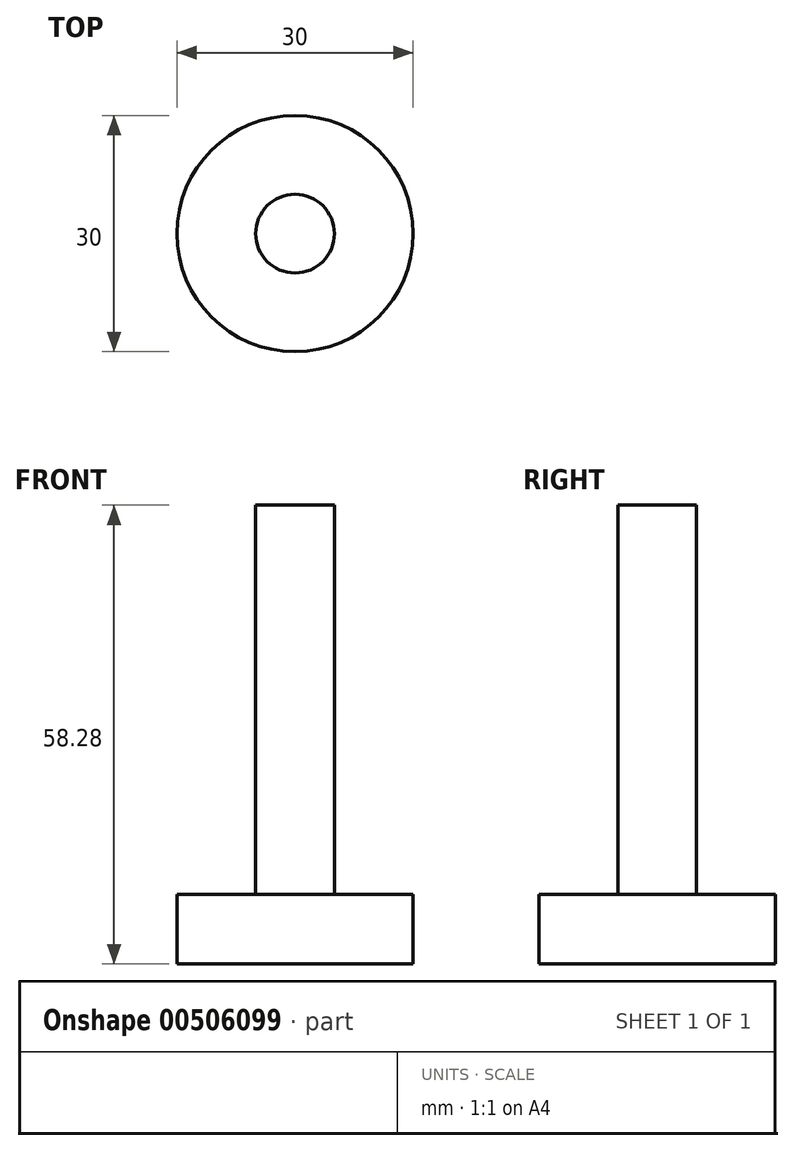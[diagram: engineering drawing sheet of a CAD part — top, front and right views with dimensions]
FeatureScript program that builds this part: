
annotation { "Feature Type Name" : "Feature", "Feature Type Description" : "" }
export const myFeature = defineFeature(function(context is Context, id is Id, definition is map)
    precondition{}
    {
        {
            var Q0;
            Q0=qCreatedBy(makeId("Front.planeOp"),FACE);
            var sketch = newSketch(context, id + "F0", { "sketchPlane" : qUnion([Q0])});
            skLineSegment(sketch, "E0", {"start": v(0, 8.63) * mm, "end": v(0, 58.28) * mm});
            skLineSegment(sketch, "E1", {"start": v(0, 58.28) * mm, "end": v(5, 58.28) * mm});
            skLineSegment(sketch, "E2", {"start": v(5, 58.28) * mm, "end": v(5, 8.84) * mm});
            skLineSegment(sketch, "E3", {"start": v(5, 8.84) * mm, "end": v(15, 8.84) * mm});
            skLineSegment(sketch, "E4", {"start": v(15, 8.84) * mm, "end": v(15, 0) * mm});
            skLineSegment(sketch, "E5", {"start": v(15, 0) * mm, "end": v(0, 0) * mm});
            skLineSegment(sketch, "E6", {"start": v(0, 0) * mm, "end": v(0, 8.63) * mm});
            skSolve(sketch);
        }
        {
            var Q0;
            Q0=makeQuery(id+"F0.imprint","IMPRINT",FACE,{"disambiguationData":[TD([[makeQuery(id+"F0.imprint","IMPRINT",EDGE,{"derivedFrom":sQuery(id+"F0.wireOp",EDGE,"E0")}),-1.0]])]});
            var Q1;
            Q1=sQuery(id+"F0.wireOp",EDGE,"E0");
            revolve(context, id + "F1", {"entities" : qUnion([Q0]), "axis" : qUnion([Q1]), "revolveType" : RevolveType.FULL});
        }
    });
